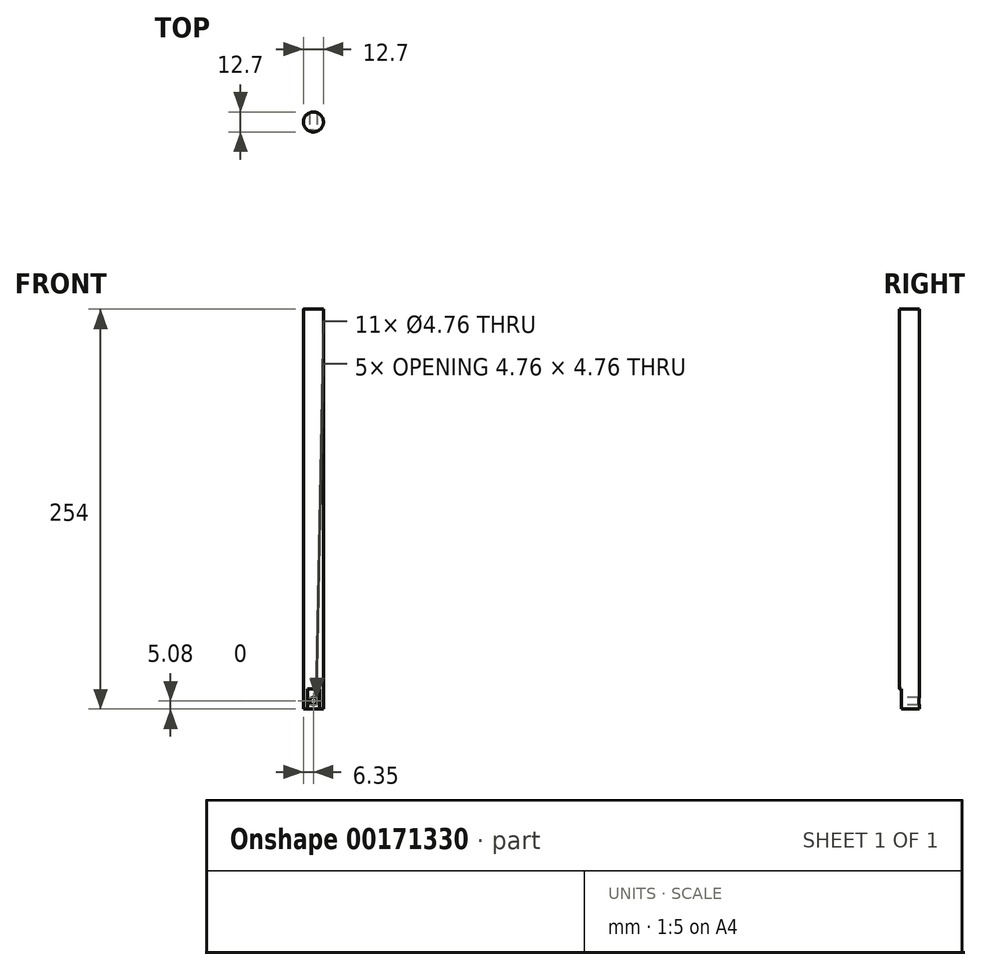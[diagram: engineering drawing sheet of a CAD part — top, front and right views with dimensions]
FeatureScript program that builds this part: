
annotation { "Feature Type Name" : "Feature", "Feature Type Description" : "" }
export const myFeature = defineFeature(function(context is Context, id is Id, definition is map)
    precondition{}
    {
        {
            var Q0;
            Q0=qCreatedBy(makeId("Top.planeOp"),FACE);
            var sketch = newSketch(context, id + "F0", { "sketchPlane" : qUnion([Q0])});
            skCircle(sketch, "E0", {"center": v(0, 0) * mm, "radius": 6.35 * mm});
            skSolve(sketch);
        }
        {
            var Q0;
            Q0 = qSketchRegion(id + "F0", true);
            extrude(context, id + "F1", {"entities" : qUnion([Q0]), "depth" : 254 * mm});
        }
        {
            var Q0;
            Q0=qCreatedBy(makeId("Front.planeOp"),FACE);
            var sketch = newSketch(context, id + "F2", { "sketchPlane" : qUnion([Q0])});
            skCircle(sketch, "E1", {"center": v(0, 5.08) * mm, "radius": 2.38 * mm});
            skSolve(sketch);
        }
        {
            var Q0;
            Q0 = qSketchRegion(id + "F2", true);
            extrude(context, id + "F3", {"entities" : qUnion([Q0]), "operationType" : NewBodyOperationType.REMOVE, "endBound" : BoundingType.SYMMETRIC, "oppositeDirection" : true, "depth" : 25.4 * mm});
        }
        {
            var Q0;
            Q0=makeQuery(id+"F1.opExtrude","CAP_FACE",FACE,{"disambiguationData":[OSD([sQuery(id+"F0.wireOp",EDGE,"E0")])],"isStart":true});
            var sketch = newSketch(context, id + "F4", { "sketchPlane" : qUnion([Q0])});
            skLineSegment(sketch, "E2.bottom", {"start": v(-20.85, 5.08) * mm, "end": v(17.42, 5.08) * mm});
            skLineSegment(sketch, "E2.top", {"start": v(-20.85, 19.08) * mm, "end": v(17.42, 19.08) * mm});
            skLineSegment(sketch, "E2.left", {"start": v(-20.85, 19.08) * mm, "end": v(-20.85, 5.08) * mm});
            skLineSegment(sketch, "E2.right", {"start": v(17.42, 19.08) * mm, "end": v(17.42, 5.08) * mm});
            skSolve(sketch);
        }
        {
            var Q0;
            Q0 = qSketchRegion(id + "F4", true);
            extrude(context, id + "F5", {"entities" : qUnion([Q0]), "operationType" : NewBodyOperationType.REMOVE, "oppositeDirection" : true, "depth" : 12.7 * mm});
        }
    });
